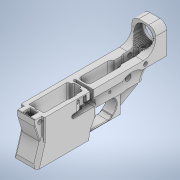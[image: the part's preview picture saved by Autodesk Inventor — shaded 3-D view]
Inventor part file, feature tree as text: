
AUTODESK INVENTOR PART (.ipt)
format: ipt  version: 2020 (Build 240168000, 168)  size: 2,544,640 bytes
history: native  units: in
note: dims shown in document units (in); Inventor stores cm internally (conversion verified against a paired STEP export)
features: extrude x1, sketch x1
ambient origin geometry x8: Origin, YZ Plane, XZ Plane, XY Plane, X Axis, Y Axis, Z Axis, Center Point
bodies: Solid1 (feature_tree), Solid2 (feature_tree)
feature tree (2):
  extrude  "Extrusion1"  [1 undecoded]
  sketch  "Sketch1"  dims[d1=1.0in d2=0.0in]
note: 1 required parameter value undecoded (feature->parameter linkage not recoverable at this tier; creation-order binding heuristic only, values carry confidence <= 0.55)
